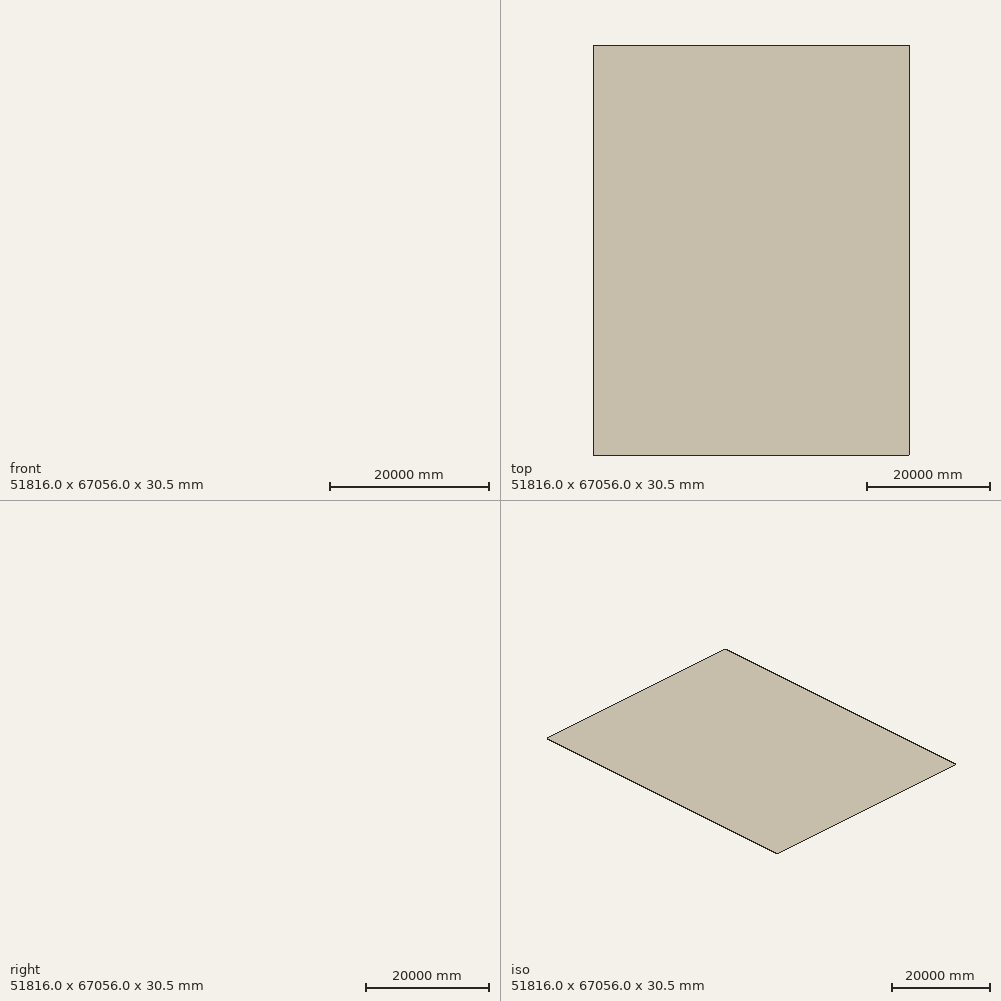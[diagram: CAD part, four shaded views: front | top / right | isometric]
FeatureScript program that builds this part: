
annotation { "Feature Type Name" : "Feature", "Feature Type Description" : "" }
export const myFeature = defineFeature(function(context is Context, id is Id, definition is map)
    precondition{}
    {
        {
            var Q0;
            Q0=qCreatedBy(makeId("Top.planeOp"),FACE);
            var sketch = newSketch(context, id + "F0", { "sketchPlane" : qUnion([Q0])});
            skLineSegment(sketch, "E0.bottom", {"start": v(0, 0) * mm, "end": v(51816, 0) * mm});
            skLineSegment(sketch, "E0.top", {"start": v(0, 67056) * mm, "end": v(51816, 67056) * mm});
            skLineSegment(sketch, "E0.left", {"start": v(0, 0) * mm, "end": v(0, 67056) * mm});
            skLineSegment(sketch, "E0.right", {"start": v(51816, 0) * mm, "end": v(51816, 67056) * mm});
            skSolve(sketch);
        }
        {
            var Q0;
            Q0 = qSketchRegion(id + "F0", true);
            extrude(context, id + "F1", {"entities" : qUnion([Q0]), "depth" : 30.48 * mm});
        }
    });
